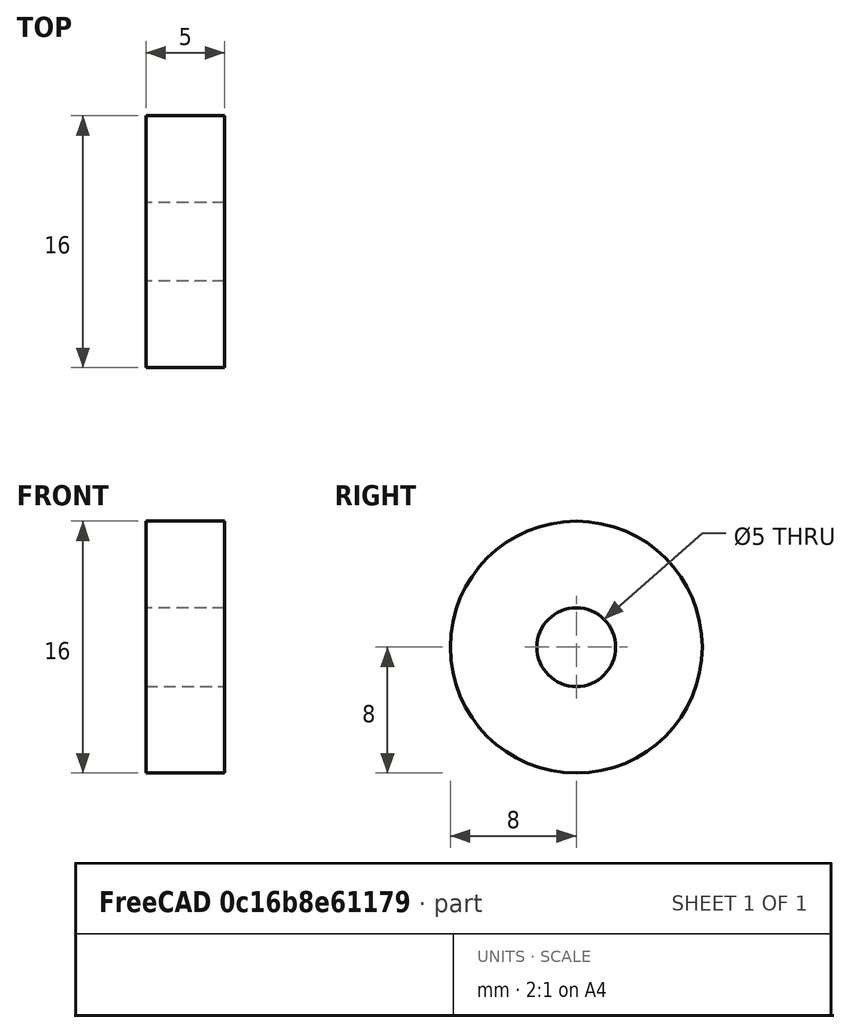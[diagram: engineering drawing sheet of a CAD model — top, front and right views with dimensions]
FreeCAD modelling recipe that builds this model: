
FCSTD DOCUMENT  (FreeCAD 2024.1R35694 (Git))
Label: bearing625
License: All rights reserved
LicenseURL: http://en.wikipedia.org/wiki/All_rights_reserved
objects: Sketcher::SketchObject×1, PartDesign::Pad×1, PartDesign::Body×1, App::Part×1
note: 4 computed .brp shape members not serialized (recipe doc carries the construction recipe); baked Part::Feature solids carry a one-line shape summary decoded from their .brp

FEATURE [Sketcher::SketchObject] Sketch
  FullyConstrained = false
  MapMode = 5
  Support = -> [XY_Plane]
  sketch-geometry (2):
    g0: Circle CenterX=0 CenterY=0 CenterZ=0 NormalX=0 NormalY=0 NormalZ=1 AngleXU=0 Radius=2.5
    g1: Circle CenterX=0 CenterY=0 CenterZ=0 NormalX=0 NormalY=0 NormalZ=1 AngleXU=0 Radius=8
  constraints (4):
    c: Coincident(g0,g-1)
    c: Coincident(g1,g0)
    c: Diameter(g0) = 5
    c: Diameter(g1) = 16
FEATURE [PartDesign::Pad] Pad
  Direction = (1,1,1)
  Length = 5
  Length2 = 100
  Profile = -> Sketch
  Type = 0
FEATURE [PartDesign::Body] Body  label="bearing625"
  Group = -> [Sketch,Pad]
  Origin = -> Origin
  Placement = pos=(0,0,0) rot=(0,-1,0;4.71239rad)
  Tip = -> Pad
FEATURE [App::Part] Part  label="b625"
  Group = -> [Body]
  Origin = -> Origin001
